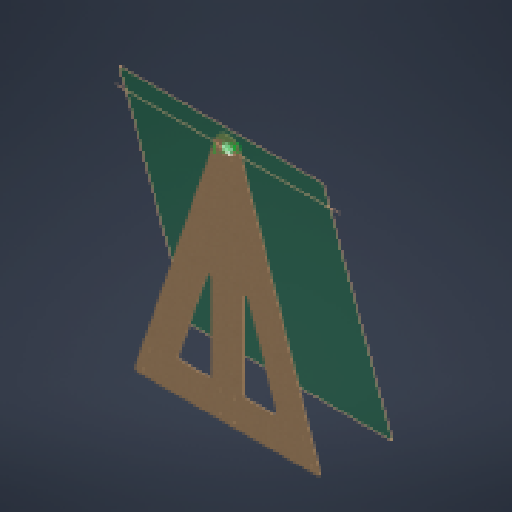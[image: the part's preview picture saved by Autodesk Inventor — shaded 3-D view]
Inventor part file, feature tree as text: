
AUTODESK INVENTOR PART (.ipt)
format: ipt  version: 2024.1 (Build 281209000, 209)  size: 217,088 bytes
history: native  units: in
note: dims shown in document units (in); Inventor stores cm internally (conversion verified against a paired STEP export)
features: other x6, sketch x3, extrude x2, fillet x1, plane x1, reference x1
ambient origin geometry x8: Origin, YZ Plane, XZ Plane, XY Plane, X Axis, Y Axis, Z Axis, Center Point
bodies: Solid1 (feature_tree)
feature tree (14):
  extrude  "Extrusion1"  Depth=18.0in
  fillet  "Fillet1"  Radius=24.0in
  plane  "Work Plane1"
  sketch  "Sketch2"  dims[d3=3.0in d4=3.0in]
  extrude  "Extrusion2"  Depth=3.0in
  sketch  "Sketch1"  dims[d0=2.5in d1=18.0in d2=24.0in]
  reference  "Reference1"
  other  "Work Point1"
  other  "Work Point2"
  other  "Work Axis1"
  sketch  "Sketch3"  dims[d5=1.5in d6=0.1575in d7=0.1575in d8=0.1575in d9=0.1575in d10=0.5in d11=0.5in d12=0.75in d13=0.75in d14=0.75in d15=0.1575in d16=0.7in d17=2.3622in d19=360.0deg d21=0.125in d22=0.0in d23=0.25in d24=15.0deg d26=1.0in d27=0.0in d28=0.0in]
  other  "<userpath>\Documents\School\FallCAD\Trebuchet\Trebuchet.iam"
  other  "Trebuchet.iam"
  other  "BallBearing_8x22x7mm:7"
